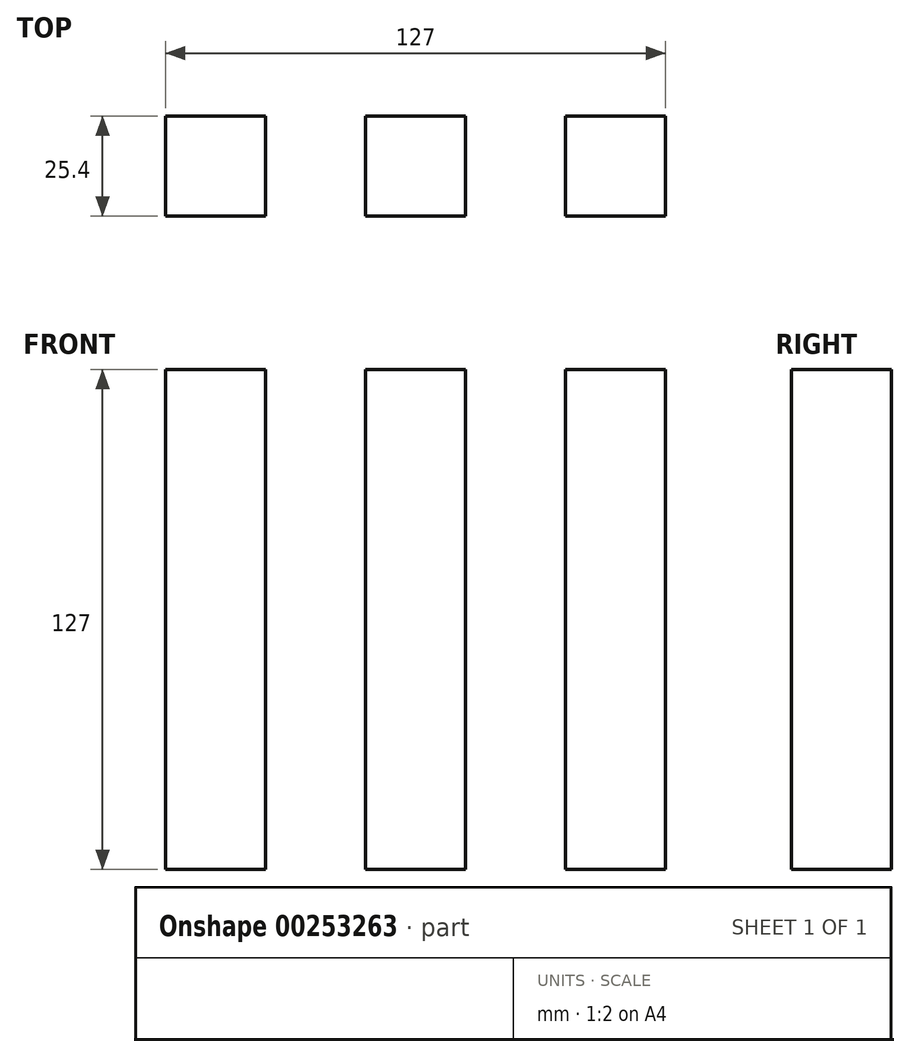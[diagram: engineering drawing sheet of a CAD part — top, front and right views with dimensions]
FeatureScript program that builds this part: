
annotation { "Feature Type Name" : "Feature", "Feature Type Description" : "" }
export const myFeature = defineFeature(function(context is Context, id is Id, definition is map)
    precondition{}
    {
        {
            var Q0;
            Q0=qCreatedBy(makeId("Top.planeOp"),FACE);
            var sketch = newSketch(context, id + "F0", { "sketchPlane" : qUnion([Q0])});
            skLineSegment(sketch, "E0.bottom", {"start": v(12.7, -12.7) * mm, "end": v(-12.7, -12.7) * mm});
            skLineSegment(sketch, "E0.top", {"start": v(12.7, 12.7) * mm, "end": v(-12.7, 12.7) * mm});
            skLineSegment(sketch, "E0.left", {"start": v(12.7, -12.7) * mm, "end": v(12.7, 12.7) * mm});
            skLineSegment(sketch, "E0.right", {"start": v(-12.7, -12.7) * mm, "end": v(-12.7, 12.7) * mm});
            skPoint(sketch, "E0.middle", {"position": v(0, 0) * mm});
            skLineSegment(sketch, "E1.bottom", {"start": v(-38.1, -12.7) * mm, "end": v(-63.5, -12.7) * mm});
            skLineSegment(sketch, "E1.top", {"start": v(-38.1, 12.7) * mm, "end": v(-63.5, 12.7) * mm});
            skLineSegment(sketch, "E1.left", {"start": v(-38.1, -12.7) * mm, "end": v(-38.1, 12.7) * mm});
            skLineSegment(sketch, "E1.right", {"start": v(-63.5, -12.7) * mm, "end": v(-63.5, 12.7) * mm});
            skPoint(sketch, "E1.middle", {"position": v(-50.8, 0) * mm});
            skLineSegment(sketch, "E2.bottom", {"start": v(63.5, -12.7) * mm, "end": v(38.1, -12.7) * mm});
            skLineSegment(sketch, "E2.top", {"start": v(63.5, 12.7) * mm, "end": v(38.1, 12.7) * mm});
            skLineSegment(sketch, "E2.left", {"start": v(63.5, -12.7) * mm, "end": v(63.5, 12.7) * mm});
            skLineSegment(sketch, "E2.right", {"start": v(38.1, -12.7) * mm, "end": v(38.1, 12.7) * mm});
            skPoint(sketch, "E2.middle", {"position": v(50.8, 0) * mm});
            skSolve(sketch);
        }
        {
            var Q0;
            Q0 = qSketchRegion(id + "F0", true);
            extrude(context, id + "F1", {"entities" : qUnion([Q0]), "depth" : 127 * mm});
        }
    });
